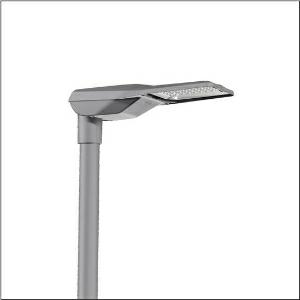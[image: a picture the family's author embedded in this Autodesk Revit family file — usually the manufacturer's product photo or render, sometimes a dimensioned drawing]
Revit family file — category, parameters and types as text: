
# Revit family: streetlight_sl_21_iq_mini___st1_0ab_5xe2m31d08gb_7ae7
name_source: partatom
category: Lighting Fixtures
units: mm (PartAtom-declared; Revit-internal decimal feet)

## family parameters
Cut with Voids When Loaded = No
Host = Face
Light Source = No
Part Type = Normal
Room Calculation Point = No
Round Connector Dimension = Use Diameter
Shared = No

## types (1)
- --- (1 x LED, 5000 lm, 37.1 W, 3000K)
    Apparent Load = 37 VA
    CIE Flux Codes = 38 73 97 100 100
    Color Rendering = 70
    Color Temperature = 3000K
    Default Elevation = 1800 mm
    Description = Streetlight SL 21 iQ mini, mast luminaire, primary light control with lens, of PMMA, primary optical cover: cover, of toughened safety glass, transparent, light distribution: ST1.0aB, light emission: direct distribution, primary light characteristic: asymmetric, installation type: post-top, side-entry, LED, High Power LED, rated luminous flux: 5.000lm, luminous efficacy: 135lm/W, light colour: 730, colour temperature: 3000K, control gear: iQ-Comfort, control: Auto-Match, Temp-Guard, Lumen-Switch, Night-Set, Smart-Wire, Light-Fading, Desk-Remote (wireless, voltage-free reading and setting of iQ features in the workshop via application-optimized NFC function/RFID function), optimised constant luminous flux control (CLO 2.0), pre-setting: linear dimming characteristic, mains connection: 220..240V, AC, 50/60Hz, start of lifetime: 37W, end of service life: 39W, reduction: 18W, luminaire housing, of diecast aluminium, powder-coated, Siteco® metallic grey (DB 702S), corrosivity category C5 mid according to DIN EN ISO 12944, please order mast flange separately, inclination adjustable: 0°, 5°, 10°, 15°, sealing non-destructively replaceable, multi-level sealing system, length: 628mm, width: 235mm, height: 110mm, mast flange for spigot size: 42mm (side-entry): 5XC10008XM4, 60/48mm (side-entry/post-top): 5XC10108XM2, 76/60mm (side-entry/post-top): 5XC10108XM1, mounting height: 4..8m, protection rating (complete): IP66, insulation class (complete): insulation class II (safety insulation), certification: CE, ENEC, ENEC+, VDE, impact resistance: IK10, permissible operating ambient temperature for outdoor applications: -40..+50°C, standard-compliant lighting for roads and squares, packaging unit: 1 piece

Light Distribution: ST1.0aB
    Height = 110 mm
    Lamp = 1 x LED
    Lamp Light Flux = 5000 lm
    Lamp Power = 37.1 W
    Lamp count = 1
    Length = 625 mm
    Luminous efficacy = 135 lm/W
    Manufacturer = Siteco
    ModVariant = No
    Model = 5XE2M31D08GB
    Number of Poles = 1
    OnlyDefault = Yes
    Power Factor = 1
    Product Name = Streetlight SL 21 iQ mini | ST1.0aB
    Product group = mast luminaire | pylon top
    ProductGroupID = 6100
    Protection Class = Protection class II
    Protection Degree = IP 66
    RLX_Detail_Level = 1
    RLX_Emergency_Light_Flux = 0 lm
    RLX_Emergency_Type = 0
    RLX_Emergency_Type_DB = No
    RlxData = <blob elided: 26297 chars, md5=c8674ac9>
    Socket = socket
    Standby Power = 0 W
    System Light Flux = 5000 lm
    System Power = 37 W
    Type Comments = factory setting: luminous flux: 100 % | dim-lin: 254 | 385 mA
    Type Image = l_1003519.jpg
    URL = http://relux.com
    VarID = @adj_204067
    Voltage = 0 V
    Weight = 0.00 kg
    Width = 234 mm

## geometry (parser evidence)
native form markers: Blend x4, Sweep x9
no freeform markers — native parametric forms only
